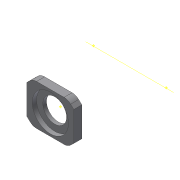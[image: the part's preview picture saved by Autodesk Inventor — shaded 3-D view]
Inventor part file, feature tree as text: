
AUTODESK INVENTOR PART (.ipt)
format: ipt  version: 2018 (Build 220112000, 112)  size: 718,848 bytes
history: native  units: mm
features: sketch x38, projected_geometry x37, extrude x33, other x10, chamfer x7, fillet x5, hole x3, reference x3, mirror x1, plane x1
ambient origin geometry x8: Origin, YZ Plane, XZ Plane, XY Plane, X Axis, Y Axis, Z Axis, Center Point
bodies: Solid1 (feature_tree)
feature tree (138):
  extrude  "Extrusion1"  Depth=45.0mm
  extrude  "Extrusion2"  Depth=2.25mm
  hole  "Hole1"  [1 undecoded]
  hole  "Hole2"  [1 undecoded]
  fillet  "Fillet1"  Radius=14.0mm
  extrude  "Extrusion3"  Depth=18.5mm
  extrude  "Extrusion4"  Depth=10.0mm
  extrude  "Extrusion5"  Depth=2.195mm
  extrude  "Extrusion6"  Depth=20.5mm
  hole  "Hole3"  [1 undecoded]
  extrude  "Extrusion7"  Depth=0.5mm
  extrude  "Extrusion8"  Depth=1.0mm TaperAngle=0.0deg
  extrude  "Extrusion9"  Depth=24.5mm
  extrude  "Extrusion10"  Depth=10.0mm
  extrude  "Extrusion11"  Depth=14.5mm
  extrude  "Extrusion13"  Depth=14.5mm
  extrude  "Extrusion14"  Depth=5.0mm
  extrude  "Extrusion15"  Depth=2.25mm
  extrude  "Extrusion16"  Depth=5.0mm
  extrude  "Extrusion17"  Depth=9.0mm
  chamfer  "Chamfer1"  Distance=1.0mm
  fillet  "Fillet7"  Radius=20.7mm
  fillet  "Fillet8"  Radius=32.0mm
  mirror  "Mirror1"
  sketch  "Sketch26"  dims[d55=2.25mm d56=5.0mm]
  extrude  "Extrusion24"  Depth=1.0mm TaperAngle=0.0deg
  extrude  "Extrusion25"  Depth=8.0mm
  extrude  "Extrusion26"  Depth=0.2mm TaperAngle=0.0deg
  extrude  "Extrusion27"  Depth=5.0mm TaperAngle=0.0deg
  other  "Work Axis1"
  plane  "Work Plane2"
  extrude  "Extrusion28"  Depth=0.2mm TaperAngle=0.0deg
  extrude  "Extrusion29"  Depth=2.5mm TaperAngle=45.0deg
  chamfer  "Chamfer2"  Distance=15.0mm
  extrude  "Extrusion31"  Depth=10.0mm TaperAngle=0.0deg
  chamfer  "Chamfer3"  Distance=15.0mm
  chamfer  "Chamfer4"  Distance=15.0mm
  extrude  "Extrusion32"  Depth=10.0mm
  chamfer  "Chamfer5"  Distance=41.5mm
  extrude  "Extrusion33"  Depth=10.0mm
  sketch  "Sketch41"  dims[d100=0.2mm d101=0.0mm d102=2.5mm d103=2.0mm d104=45.0deg]
  extrude  "Extrusion34"  Depth=10.0mm
  chamfer  "Chamfer6"  Distance=7.0mm
  fillet  "Fillet9"  Radius=100.0mm
  extrude  "Extrusion35"  Depth=10.0mm TaperAngle=0.0deg
  extrude  "Extrusion36"  Depth=10.0mm TaperAngle=45.0deg
  chamfer  "Chamfer7"  [1 undecoded]
  fillet  "Fillet10"  Radius=11.5mm
  extrude  "Extrusion37"  Depth=10.0mm
  extrude  "Extrusion38"  Depth=10.0mm
  extrude  "Extrusion40"  Depth=10.0mm TaperAngle=0.0deg
  extrude  "Extrusion41"  Depth=10.0mm TaperAngle=45.0deg
  extrude  "Extrusion42"  Depth=10.0mm TaperAngle=45.0deg
  sketch  "Sketch1"  dims[d0=24.5mm d1=45.0mm]
  sketch  "Sketch2"  dims[d2=1.95mm d3=0.0mm d4=2.25mm]
  projected_geometry  "Projected Loop1"
  sketch  "Sketch3"  dims[d5=20.0mm d6=2.25mm]
  projected_geometry  "Projected Loop2"
  sketch  "Sketch4"  dims[d7=5.25mm d8=5.25mm d9=14.0mm]
  projected_geometry  "Projected Loop3"
  sketch  "Sketch5"  dims[d10=5.25mm d11=18.5mm]
  projected_geometry  "Projected Loop4"
  sketch  "Sketch6"  dims[d12=10.0mm d13=0.0mm d14=20.5mm]
  projected_geometry  "Projected Loop5"
  sketch  "Sketch7"  dims[d15=2.0mm d16=2.195mm]
  projected_geometry  "Projected Loop6"
  sketch  "Sketch8"  dims[d17=2.0mm]
  projected_geometry  "Projected Loop7"
  sketch  "Sketch9"  dims[d18=2.4mm d19=6.0mm d20=4.4mm d21=2.0mm d22=90.0deg d23=8.0mm d24=20.594885mm d25=20.5mm]
  projected_geometry  "Projected Loop8"
  projected_geometry  "Projected Loop9"
  sketch  "Sketch10"  dims[d26=26.65mm d27=2.0mm]
  projected_geometry  "Projected Loop10"
  projected_geometry  "Projected Loop11"
  sketch  "Sketch11"  dims[d28=2.0mm]
  projected_geometry  "Projected Loop12"
  sketch  "Sketch12"  dims[d29=2.4mm d30=6.0mm d31=4.4mm d32=2.0mm d33=90.0deg d34=8.0mm d35=20.594885mm d36=0.5mm]
  sketch  "Sketch13"  dims[d37=18.0mm d38=1.0mm d39=0.0mm]
  sketch  "Sketch14"  dims[d41=5.0mm d42=0.0mm d43=24.5mm]
  projected_geometry  "Projected Loop13"
  sketch  "Sketch16"  dims[d44=1.15mm d45=0.0mm d46=10.0mm]
  projected_geometry  "Projected Loop14"
  sketch  "Sketch17"  dims[d47=21.0mm d48=14.5mm]
  projected_geometry  "Projected Loop15"
  sketch  "Sketch18"  dims[d49=20.0mm d50=14.5mm]
  projected_geometry  "Projected Loop16"
  sketch  "Sketch19"  dims[d51=24.5mm d52=5.0mm]
  projected_geometry  "Projected Loop17"
  sketch  "Sketch20"  dims[d53=5.0mm d54=2.25mm]
  projected_geometry  "Projected Loop18"
  projected_geometry  "Projected Loop25"
  sketch  "Sketch31"  dims[d57=5.0mm d58=9.0mm]
  projected_geometry  "Projected Loop30"
  reference  "Reference1"
  sketch  "Sketch32"  dims[d59=14.75mm]
  projected_geometry  "Projected Loop31"
  sketch  "Sketch33"  dims[d60=4.0mm d61=1.0mm d62=0.0mm d63=20.7mm]
  projected_geometry  "Projected Loop32"
  sketch  "Sketch34"  dims[d64=2.4mm d65=6.0mm d66=4.4mm d67=2.0mm d68=90.0deg d69=8.0mm d70=20.594885mm d72=32.0mm]
  projected_geometry  "Projected Loop33"
  other  "Work Point1"
  other  "Work Point2"
  other  "Work Point3"
  sketch  "Sketch35"  dims[d73=3.0mm d74=0.0mm d75=1.0mm d76=0.0mm]
  sketch  "Sketch37"  dims[d77=12.25mm d78=0.0mm d80=8.0mm]
  projected_geometry  "Projected Loop34"
  sketch  "Sketch38"  dims[d81=4.5mm d82=0.0mm d84=0.2mm d85=0.0mm]
  sketch  "Sketch39"  dims[d91=8.0mm d92=0.0mm d93=5.0mm d94=0.0mm]
  sketch  "Sketch40"  dims[d95=5.0mm d96=0.0mm d98=0.2mm d99=0.0mm]
  projected_geometry  "Projected Loop35"
  projected_geometry  "Projected Loop36"
  projected_geometry  "Projected Loop37"
  projected_geometry  "Projected Loop38"
  sketch  "Sketch42"  dims[d105=1.5mm]
  projected_geometry  "Projected Loop39"
  sketch  "Sketch43"  dims[d114=0.5mm]
  reference  "Reference2"
  reference  "Reference3"
  sketch  "Sketch45"  dims[d130=60.0mm]
  projected_geometry  "Projected Loop40"
  sketch  "Sketch46"  dims[d131=36.0mm]
  projected_geometry  "Projected Loop41"
  sketch  "Sketch48"  dims[d146=40.0mm]
  projected_geometry  "Projected Loop43"
  sketch  "Sketch50"  dims[d147=60.0mm]
  projected_geometry  "Projected Loop46"
  sketch  "Sketch53"  dims[d148=0.0mm]
  projected_geometry  "Projected Loop48"
  sketch  "Sketch55"  dims[d149=2.3mm d150=15.0mm d151=0.0mm d152=15.0mm d153=0.0mm d154=15.0mm d155=0.0mm d156=15.0mm d157=0.0mm d158=20.5mm d159=41.5mm d160=14.0mm d161=14.0mm d162=7.0mm d165=100.0mm d166=0.0mm d167=100.0mm d168=0.0mm d169=6.0mm d170=2.0mm d171=45.0deg d172=0.0mm d173=11.5mm d175=11.5mm d176=11.5mm d179=100.0mm d180=0.0mm d181=5.0mm d182=2.0mm d183=45.0deg d184=5.0mm d185=2.0mm d186=45.0deg d187=8.0mm d188=100.0mm d189=0.0mm d190=5.0mm d191=2.0mm d192=45.0deg d193=100.0mm d194=0.0mm d195=100.0mm d196=0.0mm d197=5.0mm d198=2.0mm d199=45.0deg d200=8.0mm d202=15.0deg d204=10.970628mm d205=15.470628mm d206=2.5mm d207=0.0mm d208=2.5mm d209=0.0mm d210=3.0mm d211=2.0mm d212=45.0deg d213=2.0mm d215=15.0deg d216=4.0mm d217=4.0mm d218=5.0mm d219=0.0mm d222=32.07mm d223=3.9mm d224=0.0mm d227=7.1mm d228=0.0mm d237=10.0mm d238=0.0mm d239=10.0mm d240=0.0mm]
  projected_geometry  "Projected Loop49"
  parser-record x1  (decoder bookkeeping rows leaked as tree rows — omitted from the tree; the rows remain in map.json)
  other  "servocheck.iam"
  other  "LX-16A:3"
  other  "DUOPAN-SG-SJ_10"
  projected_geometry  "Project Cut Edges1"
  projected_geometry  "Project Cut Edges3"
  other  "bottomarm:1"
  other  "arm1:1"
note: 4 required parameter values undecoded (feature->parameter linkage not recoverable at this tier; creation-order binding heuristic only, values carry confidence <= 0.55)
note: 1 file-system path scrubbed to <path> (originals preserved in map.json)
